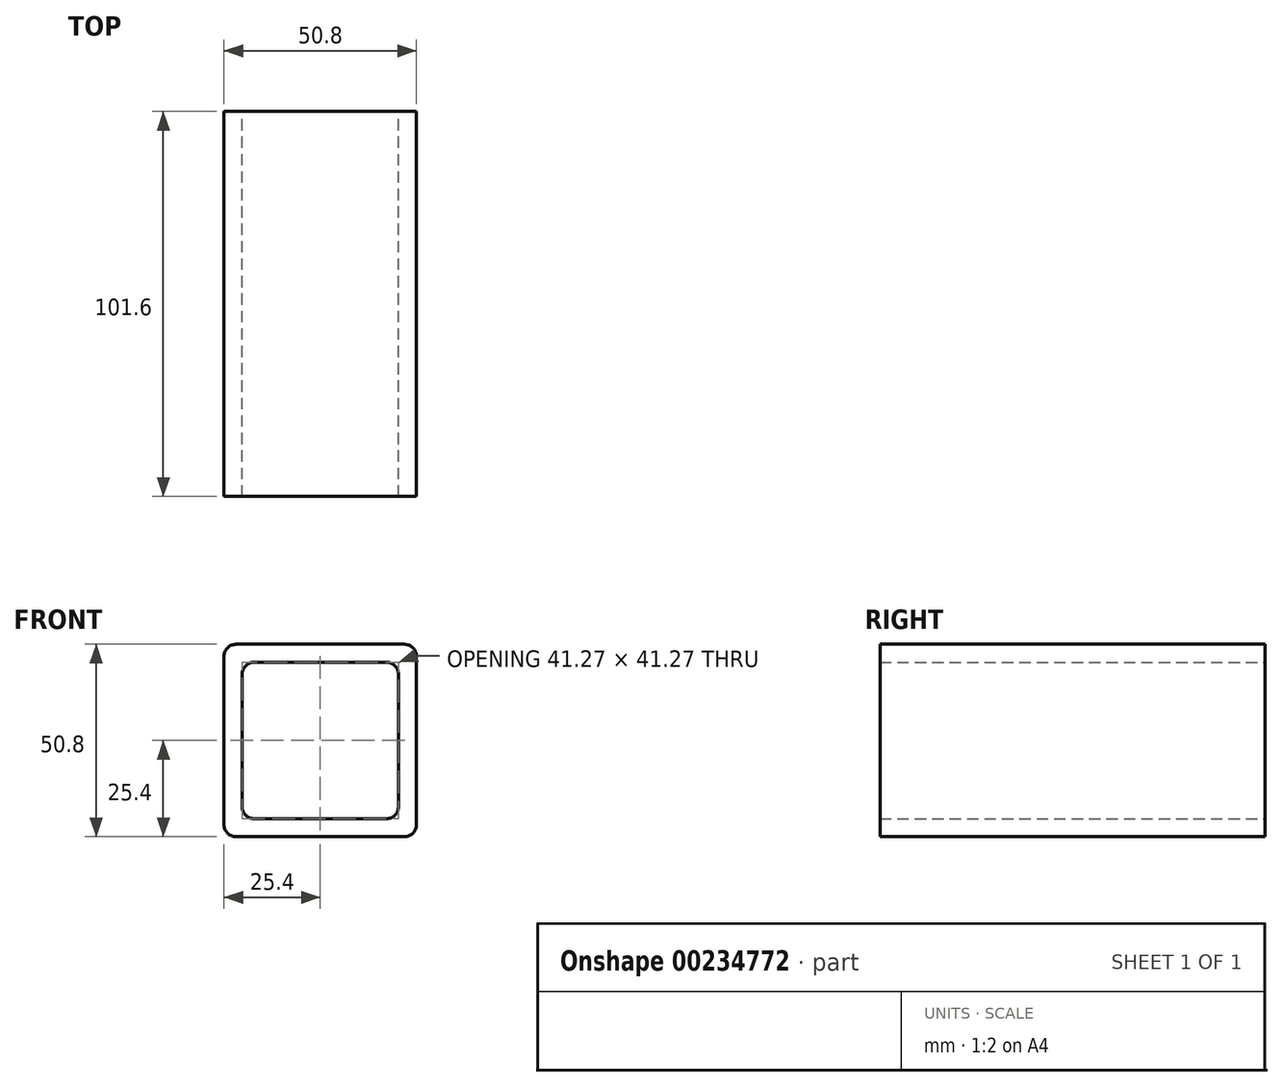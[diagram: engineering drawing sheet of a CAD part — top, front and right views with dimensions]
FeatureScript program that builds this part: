
annotation { "Feature Type Name" : "Feature", "Feature Type Description" : "" }
export const myFeature = defineFeature(function(context is Context, id is Id, definition is map)
    precondition{}
    {
        {
            var Q0;
            Q0=qCreatedBy(makeId("Front.planeOp"),FACE);
            var sketch = newSketch(context, id + "F0", { "sketchPlane" : qUnion([Q0])});
            skLineSegment(sketch, "E0.bottom", {"start": v(22.23, -25.4) * mm, "end": v(-22.23, -25.4) * mm});
            skLineSegment(sketch, "E0.top", {"start": v(22.23, 25.4) * mm, "end": v(-22.23, 25.4) * mm});
            skLineSegment(sketch, "E0.left", {"start": v(25.4, -22.23) * mm, "end": v(25.4, 22.23) * mm});
            skLineSegment(sketch, "E0.right", {"start": v(-25.4, -22.23) * mm, "end": v(-25.4, 22.23) * mm});
            skPoint(sketch, "E0.middle", {"position": v(0, 0) * mm});
            skLineSegment(sketch, "E1.bottom", {"start": v(17.46, -20.64) * mm, "end": v(-17.46, -20.64) * mm});
            skLineSegment(sketch, "E1.top", {"start": v(17.46, 20.64) * mm, "end": v(-17.46, 20.64) * mm});
            skLineSegment(sketch, "E1.left", {"start": v(20.64, -17.46) * mm, "end": v(20.64, 17.46) * mm});
            skLineSegment(sketch, "E1.right", {"start": v(-20.64, -17.46) * mm, "end": v(-20.64, 17.46) * mm});
            skPoint(sketch, "E2.visualSharp", {"position": v(-25.4, 25.4) * mm});
            skArc(sketch, "E2.filletArc", {"start": v(-22.23, 25.4) * mm, "mid": v(-24.47, 24.47) * mm, "end": v(-25.4, 22.23) * mm});
            skPoint(sketch, "E3.visualSharp", {"position": v(25.4, 25.4) * mm});
            skArc(sketch, "E3.filletArc", {"start": v(25.4, 22.23) * mm, "mid": v(24.47, 24.47) * mm, "end": v(22.23, 25.4) * mm});
            skPoint(sketch, "E4.visualSharp", {"position": v(20.64, 20.64) * mm});
            skArc(sketch, "E4.filletArc", {"start": v(20.64, 17.46) * mm, "mid": v(19.7, 19.7) * mm, "end": v(17.46, 20.64) * mm});
            skPoint(sketch, "E5.visualSharp", {"position": v(-20.64, 20.64) * mm});
            skArc(sketch, "E5.filletArc", {"start": v(-17.46, 20.64) * mm, "mid": v(-19.7, 19.7) * mm, "end": v(-20.64, 17.46) * mm});
            skPoint(sketch, "E6.visualSharp", {"position": v(-20.64, -20.64) * mm});
            skArc(sketch, "E6.filletArc", {"start": v(-20.64, -17.46) * mm, "mid": v(-19.7, -19.7) * mm, "end": v(-17.46, -20.64) * mm});
            skPoint(sketch, "E7.visualSharp", {"position": v(-25.4, -25.4) * mm});
            skArc(sketch, "E7.filletArc", {"start": v(-25.4, -22.23) * mm, "mid": v(-24.47, -24.47) * mm, "end": v(-22.23, -25.4) * mm});
            skPoint(sketch, "E8.visualSharp", {"position": v(20.64, -20.64) * mm});
            skArc(sketch, "E8.filletArc", {"start": v(17.46, -20.64) * mm, "mid": v(19.7, -19.7) * mm, "end": v(20.64, -17.46) * mm});
            skPoint(sketch, "E9.visualSharp", {"position": v(25.4, -25.4) * mm});
            skArc(sketch, "E9.filletArc", {"start": v(22.23, -25.4) * mm, "mid": v(24.47, -24.47) * mm, "end": v(25.4, -22.23) * mm});
            skSolve(sketch);
        }
        {
            var Q0;
            Q0=makeQuery(id+"F0.imprint","IMPRINT",FACE,{"disambiguationData":[TD([[makeQuery(id+"F0.imprint","IMPRINT",EDGE,{"derivedFrom":sQuery(id+"F0.wireOp",EDGE,"E0.bottom")}),-1.0]])]});
            extrude(context, id + "F1", {"entities" : qUnion([Q0]), "depth" : 101.6 * mm});
        }
    });
